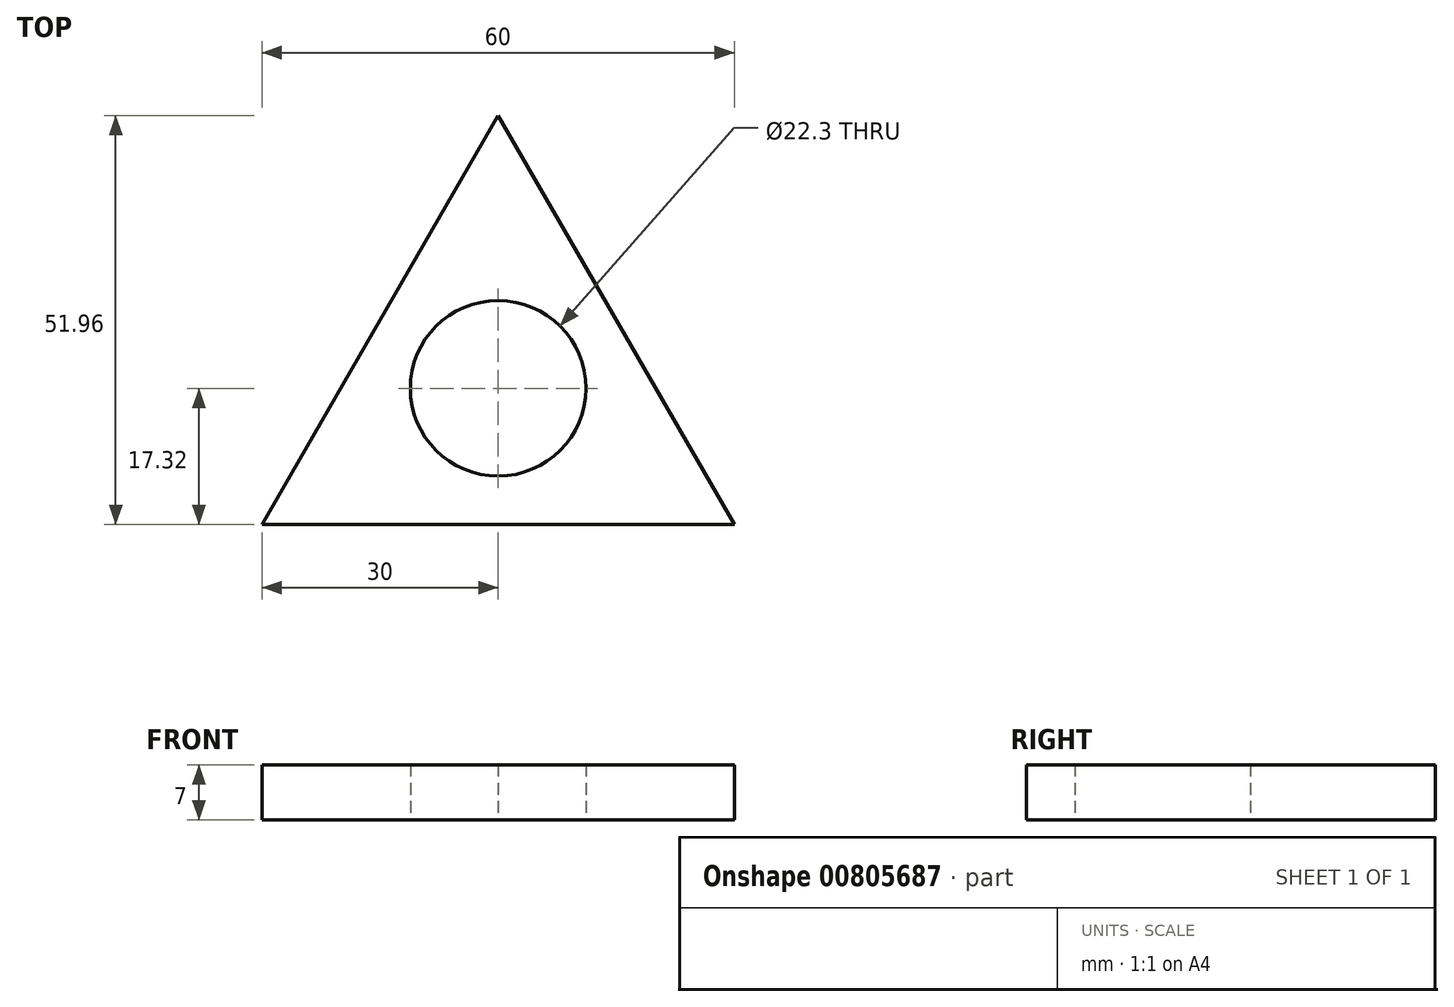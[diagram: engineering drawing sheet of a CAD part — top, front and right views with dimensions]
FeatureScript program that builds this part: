
annotation { "Feature Type Name" : "Feature", "Feature Type Description" : "" }
export const myFeature = defineFeature(function(context is Context, id is Id, definition is map)
    precondition{}
    {
        {
            var Q0;
            Q0=qCreatedBy(makeId("Top.planeOp"),FACE);
            var sketch = newSketch(context, id + "F0", { "sketchPlane" : qUnion([Q0])});
            skCircle(sketch, "E0.cCircle", {"center": v(0, 0) * mm, "radius": 17.32 * mm, "construction": true});
            skLineSegment(sketch, "E0.0", {"start": v(30, -17.32) * mm, "end": v(-30, -17.32) * mm});
            skLineSegment(sketch, "E0.1", {"start": v(-30, -17.32) * mm, "end": v(0, 34.64) * mm});
            skLineSegment(sketch, "E0.2", {"start": v(0, 34.64) * mm, "end": v(30, -17.32) * mm});
            skPoint(sketch, "E0.0.midPoint", {"position": v(0, -17.32) * mm});
            skCircle(sketch, "E1", {"center": v(0, 0) * mm, "radius": 11.15 * mm});
            skLineSegment(sketch, "E2.anchor1", {"start": v(0, 0) * mm, "end": v(-4.28, 27.23) * mm, "construction": true});
            skLineSegment(sketch, "E2.anchor2", {"start": v(0, 0) * mm, "end": v(-21.45, -17.32) * mm, "construction": true});
            skSolve(sketch);
        }
        {
            var Q0;
            Q0=makeQuery(id+"F0.imprint","IMPRINT",FACE,{"disambiguationData":[TD([[makeQuery(id+"F0.imprint","IMPRINT",EDGE,{"derivedFrom":sQuery(id+"F0.wireOp",EDGE,"E1")}),-1.0]])]});
            extrude(context, id + "F1", {"entities" : qUnion([Q0]), "depth" : 7 * mm, "offsetDistance" : 25 * mm});
        }
    });
